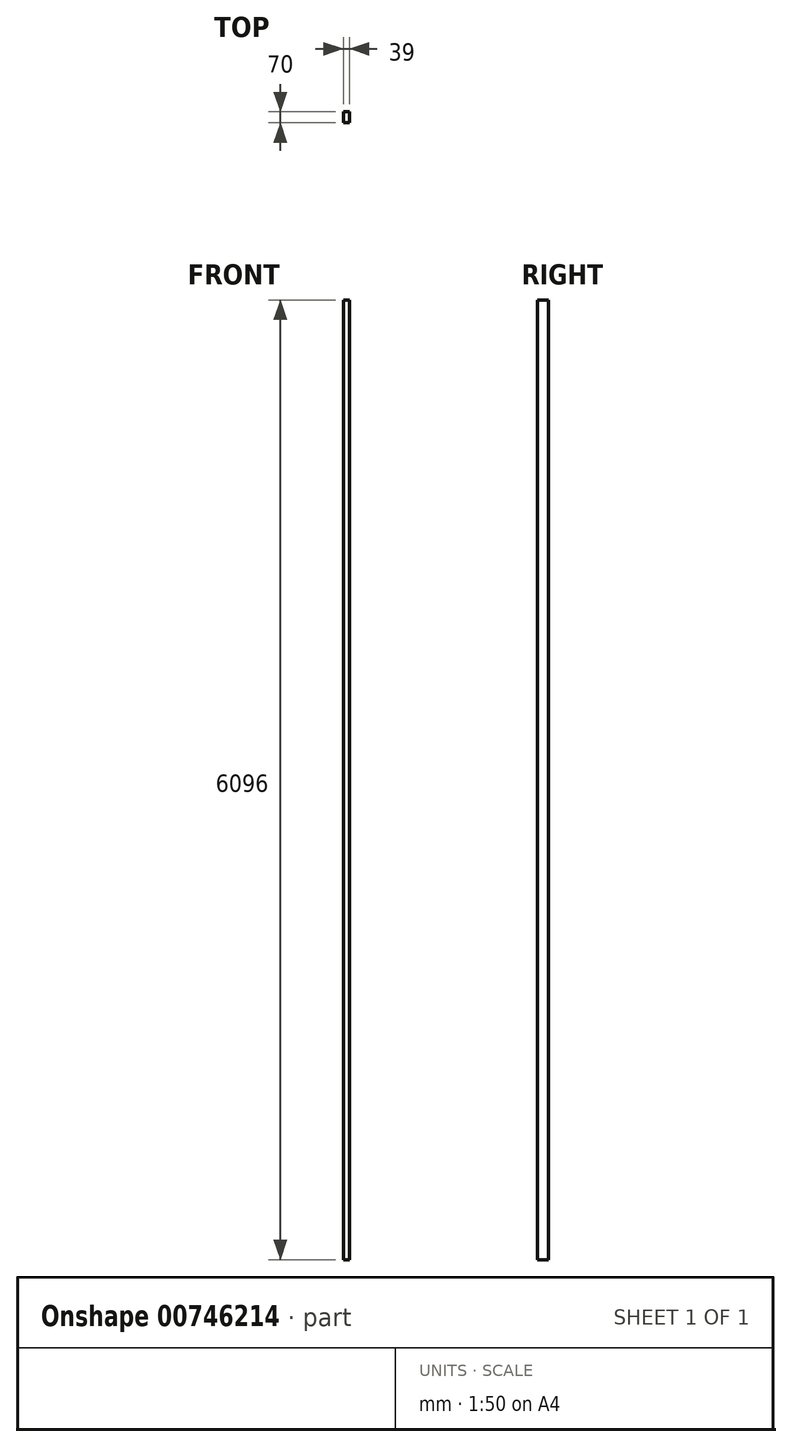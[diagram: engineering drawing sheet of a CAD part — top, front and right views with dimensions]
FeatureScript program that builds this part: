
annotation { "Feature Type Name" : "Feature", "Feature Type Description" : "" }
export const myFeature = defineFeature(function(context is Context, id is Id, definition is map)
    precondition{}
    {
        {
            var Q0;
            Q0=qCreatedBy(makeId("Top.planeOp"),FACE);
            var sketch = newSketch(context, id + "F0", { "sketchPlane" : qUnion([Q0])});
            skLineSegment(sketch, "E0.bottom", {"start": v(19.5, -35) * mm, "end": v(-19.5, -35) * mm});
            skLineSegment(sketch, "E0.top", {"start": v(19.5, 35) * mm, "end": v(-19.5, 35) * mm});
            skLineSegment(sketch, "E0.left", {"start": v(19.5, -35) * mm, "end": v(19.5, 35) * mm});
            skLineSegment(sketch, "E0.right", {"start": v(-19.5, -35) * mm, "end": v(-19.5, 35) * mm});
            skPoint(sketch, "E0.middle", {"position": v(0, 0) * mm});
            skSolve(sketch);
        }
        {
            var Q0;
            Q0=makeQuery(id+"F0.imprint","IMPRINT",FACE,{"disambiguationData":[TD([[makeQuery(id+"F0.imprint","IMPRINT",EDGE,{"derivedFrom":sQuery(id+"F0.wireOp",EDGE,"E0.bottom")}),-1.0]])]});
            extrude(context, id + "F1", {"entities" : qUnion([Q0]), "depth" : 6096 * mm, "offsetDistance" : 25.4 * mm});
        }
    });
